# Revit family: O2.5UM-NRG SUSHI_1
name_source: partatom
category: Mechanical Equipment
revit_build: Autodesk Revit 2017 (Build: 20190508_0315(x64)
units: mm (PartAtom-declared; Revit-internal decimal feet)

## family parameters
Always vertical = Yes
Cut with Voids When Loaded = No
OmniClass Number = 23.40.40.11.17
OmniClass Title = Refrigerated Cases
Part Type = Normal
Room Calculation Point = No
Round Connector Dimension = Use Radius
Shared = No
Work Plane-Based = Yes

## types (4) — shared parameters
12" Shelf = Yes
18" Shelf = Yes
Aluminum Frame = <By Category>
BOTTOM ELECTRICAL = Yes
BOTTOM REFRIGERATION PIPING = Yes
Certifications = NSF 7, UL471, CSA
DATE = 06/18/2020
DESIGNERS NAME = T.A.G
DRAIN LINE = 36"
DRAIN PIPING = Yes
Default Elevation = 48"
Description = Multi-Deck Merchandiser with Synerg-E™
EQUIPMENT DESCRIPTION = Multi-Deck Merchandiser with Synerg-E™
EQUIPMENT MARK = O2.5UM-NRG Sushi
Ends = Yes
GLASS = Glass
Glass = Glass
Height = 44 1/8"
High Power (Cornice) Amps = 0 A
High Power (Cornice) Watts = 30 W
How Many Defrosts Per Day = 6
Island  Case Length = 72"
Island Application = Dairy / Deli / Produce
Island BTUH Conventional = 858
Island BTUH Parallel = 750
Island Discharge Air Velocity (FPM) = 180 FPM
Island Discharge Air(°F) = 31 °F
Island Evaporator (°F) = 28 °F
Island Fans Per Case = 2
Island Front Sill Height = All
Island High Efficiency Fans Amps = 0 A
Island High Efficiency Fans Watts = 22 W
Island Superheat @ Bulb Set Point (°F) = 6-8 °F
Island Timed-Off Fail-Safe (Min) = 30 (Min)
Island Timed-Off Termination Temp (°F) = 42 °F
Item Description = Multi-Deck Merchandiser with Synerg-E™
LF STD END = Yes
Left KP End = No
Legend Number = O2.5UM-NRG Sushi
Light Length = 36"
Lights = CHARCOAL BROWN
Lights Per Row = 2
Manufacturer = HILL PHOENIX
Model = O2.5UM-NRG Sushi
Number of Shelf = 3
PAINTED METAL UPPER SHELF = PAINTED SHELVES
REAR REFRIGERATION PIPING = Yes
RT KP End = No
RT STD END = Yes
Refgn = 12 3/8"
Shelf distance = 36"
Standard Power Amps = 14 A
Standard Power Watts = 17 W
TOP ELECTRICAL = Yes
TOP REFRIGERATION PIPING = Yes
URL = http://www.hillphoenix.com Sushi
Width = 43 1/4"

## per-type parameters (varying)
| type | Length | Sneezeguard_1 |
| 12' | 144" | Sneezeguard_12'_2 : 12' |
| 4' | 48" | Sneezeguard_4' : 4' |
| 6' | 72" | Sneezeguard_6' : 6' |
| 8' | 96" | Sneezeguard_8' : 8' |

## geometry (parser evidence)
native form markers: Blend x11, Sweep x57
no freeform markers — native parametric forms only
